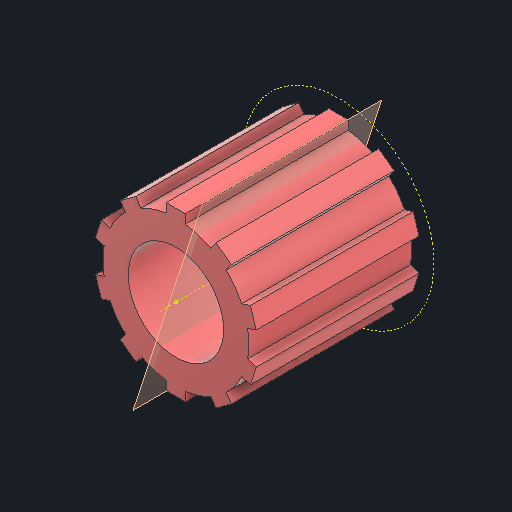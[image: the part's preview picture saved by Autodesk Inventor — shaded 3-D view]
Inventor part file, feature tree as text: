
AUTODESK INVENTOR PART (.ipt)
format: ipt  version: 2024 (Build 280153000, 153)  size: 218,112 bytes
history: native  units: in
note: dims shown in document units (in); Inventor stores cm internally (conversion verified against a paired STEP export)
features: sketch x5, other x3, plane x2
ambient origin geometry x8: Origin, YZ Plane, XZ Plane, XY Plane, X Axis, Y Axis, Z Axis, Center Point
bodies: Solid1 (feature_tree)
feature tree (10):
  other  "felga.ipt"
  other  "Solid1::felga.ipt"
  other  "TaggingFeature1"
  sketch  "Sketch1"  dims[d0=0.3937in]
  sketch  "Sketch2"
  sketch  "Sketch3"
  sketch  "Sketch4"
  sketch  "Sketch5"
  plane  "Work Plane1"
  plane  "Work Plane2"
